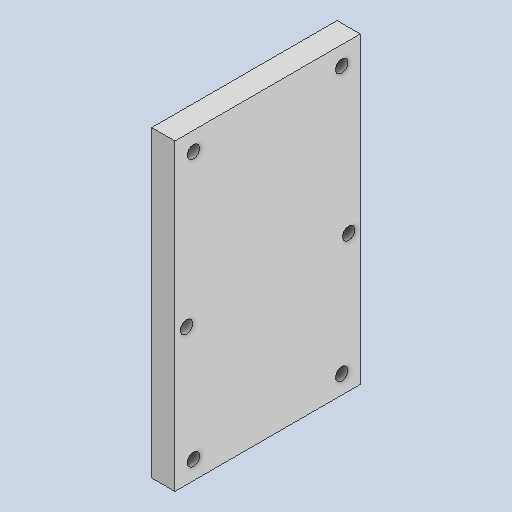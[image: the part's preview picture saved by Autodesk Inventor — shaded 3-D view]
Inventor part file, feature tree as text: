
AUTODESK INVENTOR PART (.ipt)
format: ipt  version: 2023 (Build 270158000, 158)  size: 249,344 bytes
history: native  units: in
note: dims shown in document units (in); Inventor stores cm internally (conversion verified against a paired STEP export)
features: extrude x1
ambient origin geometry x8: Origin, YZ Plane, XZ Plane, XY Plane, X Axis, Y Axis, Z Axis, Center Point
bodies: Solid1 (feature_tree)
feature tree (1):
  extrude  "Extrusion1"  Depth=3.275in
